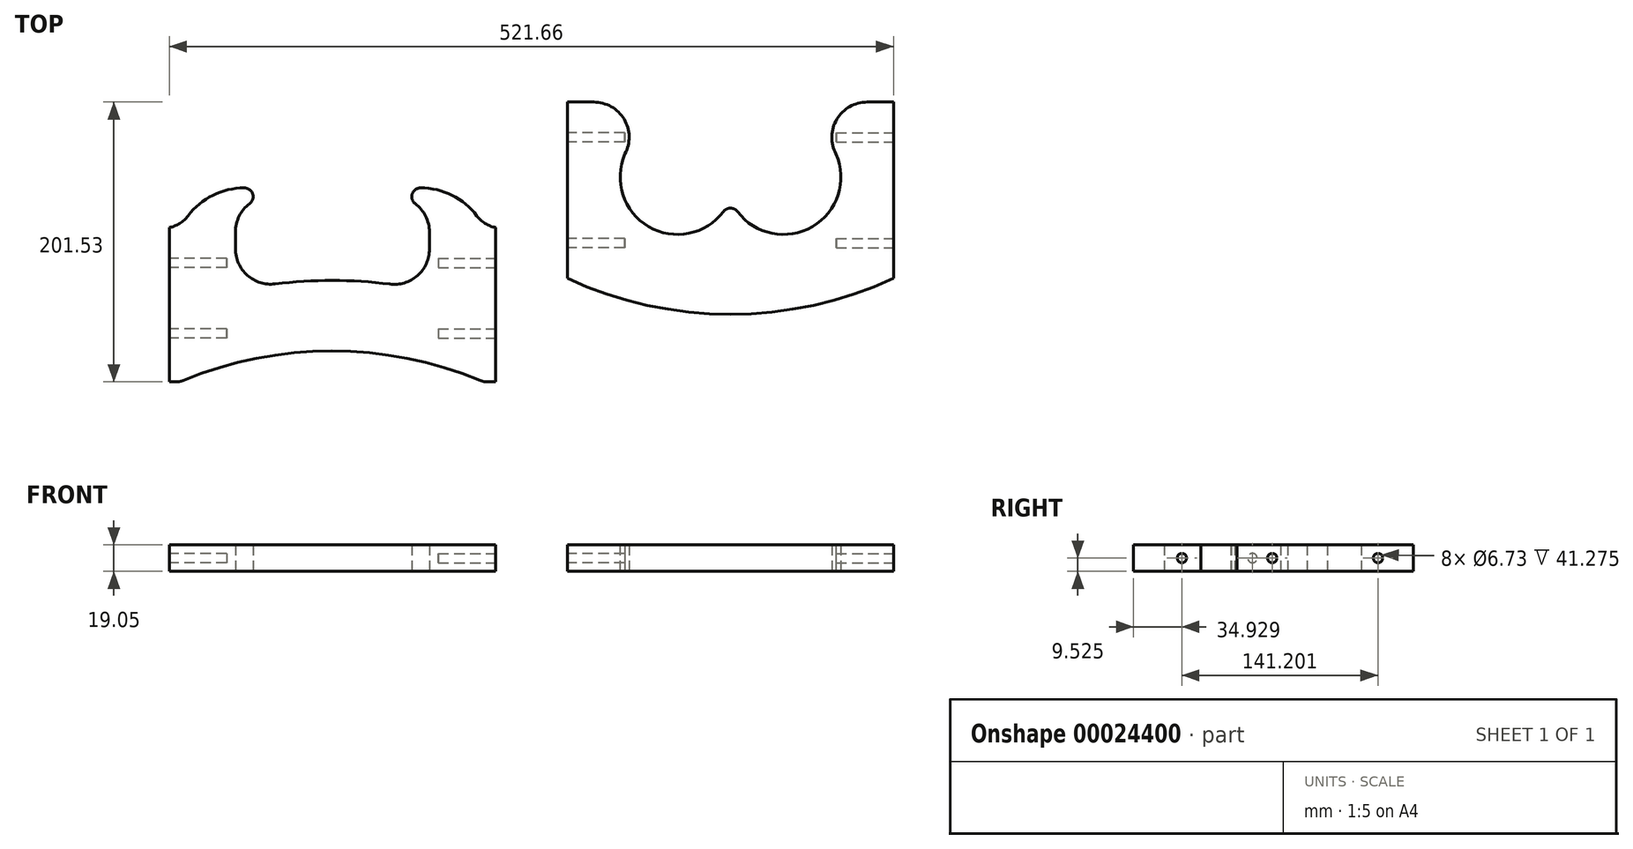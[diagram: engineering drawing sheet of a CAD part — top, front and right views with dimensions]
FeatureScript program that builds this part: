
annotation { "Feature Type Name" : "Feature", "Feature Type Description" : "" }
export const myFeature = defineFeature(function(context is Context, id is Id, definition is map)
    precondition{}
    {
        {
            var Q0;
            Q0=qCreatedBy(makeId("Top.planeOp"),FACE);
            var sketch = newSketch(context, id + "F0", { "sketchPlane" : qUnion([Q0])});
            skLineSegment(sketch, "E0.bottom", {"start": v(0, 0) * mm, "end": v(234.95, 0) * mm, "construction": true});
            skLineSegment(sketch, "E0.top", {"start": v(0, 152.4) * mm, "end": v(19.05, 152.4) * mm});
            skLineSegment(sketch, "E0.left", {"start": v(0, 0) * mm, "end": v(0, 25.4) * mm, "construction": true});
            skLineSegment(sketch, "E0.right", {"start": v(234.95, 0) * mm, "end": v(234.95, 25.4) * mm, "construction": true});
            skArc(sketch, "E1", {"start": v(41.43, 115) * mm, "mid": v(40.85, 140.04) * mm, "end": v(19.05, 152.4) * mm});
            skLineSegment(sketch, "E2", {"start": v(234.95, 143.8) * mm, "end": v(234.95, 143.8) * mm});
            skArc(sketch, "E3", {"start": v(42.52, 117.3) * mm, "mid": v(57.38, 63.35) * mm, "end": v(112.4, 73.47) * mm});
            skArc(sketch, "E4", {"start": v(122.54, 73.47) * mm, "mid": v(177.57, 63.35) * mm, "end": v(192.43, 117.3) * mm});
            skArc(sketch, "E5", {"start": v(0, 25.4) * mm, "mid": v(117.47, -0.5) * mm, "end": v(234.95, 25.4) * mm});
            skLineSegment(sketch, "E6", {"start": v(0, 25.4) * mm, "end": v(0, 143.8) * mm});
            skLineSegment(sketch, "E7", {"start": v(234.95, 25.4) * mm, "end": v(234.95, 143.8) * mm});
            skLineSegment(sketch, "E8.trimOffspring", {"start": v(215.9, 152.4) * mm, "end": v(234.95, 152.4) * mm});
            skLineSegment(sketch, "E9", {"start": v(0, 143.8) * mm, "end": v(0, 152.4) * mm});
            skArc(sketch, "E10", {"start": v(215.9, 152.4) * mm, "mid": v(194.1, 140.04) * mm, "end": v(193.52, 115) * mm});
            skLineSegment(sketch, "E11", {"start": v(234.95, 143.8) * mm, "end": v(234.95, 152.4) * mm});
            skArc(sketch, "E12", {"start": v(122.54, 73.47) * mm, "mid": v(117.48, 75.99) * mm, "end": v(112.4, 73.47) * mm});
            skLineSegment(sketch, "E13", {"start": v(117.48, 82.22) * mm, "end": v(117.48, 0) * mm, "construction": true});
            skSolve(sketch);
        }
        {
            var Q0;
            Q0 = qSketchRegion(id + "F0", true);
            extrude(context, id + "F1", {"entities" : qUnion([Q0]), "depth" : 19.05 * mm});
        }
        {
            var Q0;
            Q0=makeQuery(id+"F1.opExtrude","SWEPT_FACE",FACE,{"disambiguationData":[OSD([sQuery(id+"F0.wireOp",EDGE,"E6")])]});
            var sketch = newSketch(context, id + "F2", { "sketchPlane" : qUnion([Q0])});
            skLineSegment(sketch, "E14", {"start": v(-152.4, 9.53) * mm, "end": v(-25.4, 9.53) * mm, "construction": true});
            skCircle(sketch, "E15", {"center": v(-127, 9.53) * mm, "radius": 3.37 * mm});
            skCircle(sketch, "E16", {"center": v(-50.8, 9.53) * mm, "radius": 3.37 * mm});
            skSolve(sketch);
        }
        {
            var Q0;
            Q0=makeQuery(id+"F2.imprint","IMPRINT",FACE,{"disambiguationData":[TD([[makeQuery(id+"F2.imprint","IMPRINT",EDGE,{"derivedFrom":sQuery(id+"F2.wireOp",EDGE,"E16")}),1.0]])]});
            var Q1;
            Q1=makeQuery(id+"F2.imprint","IMPRINT",FACE,{"disambiguationData":[TD([[makeQuery(id+"F2.imprint","IMPRINT",EDGE,{"derivedFrom":sQuery(id+"F2.wireOp",EDGE,"E15")}),1.0]])]});
            var Q2;
            Q2=sQuery(id+"F2.wireOp",EDGE,"E16");
            var Q3;
            Q3=sQuery(id+"F2.wireOp",EDGE,"E15");
            extrude(context, id + "F3", {"entities" : qUnion([Q0, Q1]), "operationType" : NewBodyOperationType.REMOVE, "surfaceEntities" : qUnion([Q2, Q3]), "oppositeDirection" : true, "depth" : 41.27 * mm});
        }
        {
            var Q0;
            Q0=makeQuery(id+"F1.opExtrude","SWEPT_FACE",FACE,{"disambiguationData":[OSD([sQuery(id+"F0.wireOp",EDGE,"E7"),sQuery(id+"F0.wireOp",EDGE,"E11")])]});
            var sketch = newSketch(context, id + "F4", { "sketchPlane" : qUnion([Q0])});
            skLineSegment(sketch, "E17", {"start": v(152.4, 9.53) * mm, "end": v(25.4, 9.53) * mm, "construction": true});
            skCircle(sketch, "E18", {"center": v(127, 9.53) * mm, "radius": 3.37 * mm});
            skCircle(sketch, "E19", {"center": v(50.8, 9.52) * mm, "radius": 3.37 * mm});
            skSolve(sketch);
        }
        {
            var Q0;
            Q0=makeQuery(id+"F4.imprint","IMPRINT",FACE,{"disambiguationData":[TD([[makeQuery(id+"F4.imprint","IMPRINT",EDGE,{"derivedFrom":sQuery(id+"F4.wireOp",EDGE,"E18")}),1.0]])]});
            var Q1;
            Q1=makeQuery(id+"F4.imprint","IMPRINT",FACE,{"disambiguationData":[TD([[makeQuery(id+"F4.imprint","IMPRINT",EDGE,{"derivedFrom":sQuery(id+"F4.wireOp",EDGE,"E19")}),1.0]])]});
            extrude(context, id + "F5", {"entities" : qUnion([Q0, Q1]), "operationType" : NewBodyOperationType.REMOVE, "oppositeDirection" : true, "depth" : 41.27 * mm});
        }
        {
            var Q0;
            Q0=qCreatedBy(makeId("Top.planeOp"),FACE);
            var sketch = newSketch(context, id + "F6", { "sketchPlane" : qUnion([Q0])});
            skLineSegment(sketch, "E20.bottom", {"start": v(-286.71, -49.13) * mm, "end": v(-281.48, -49.13) * mm});
            skLineSegment(sketch, "E20.top", {"start": v(-286.71, 90.57) * mm, "end": v(-232.74, 90.57) * mm, "construction": true});
            skLineSegment(sketch, "E20.left", {"start": v(-286.71, -49.13) * mm, "end": v(-286.71, 62) * mm});
            skLineSegment(sketch, "E20.right", {"start": v(-51.76, -49.13) * mm, "end": v(-51.76, 62) * mm});
            skLineSegment(sketch, "E21", {"start": v(-286.71, 62) * mm, "end": v(-286.71, 89.56) * mm, "construction": true});
            skLineSegment(sketch, "E22", {"start": v(-51.76, 62) * mm, "end": v(-51.76, 89.56) * mm, "construction": true});
            skLineSegment(sketch, "E23.trimOffspring", {"start": v(-105.74, 90.57) * mm, "end": v(-51.76, 90.57) * mm, "construction": true});
            skLineSegment(sketch, "E24", {"start": v(-286.71, 89.56) * mm, "end": v(-286.71, 90.57) * mm});
            skLineSegment(sketch, "E25", {"start": v(-51.76, 89.56) * mm, "end": v(-51.76, 90.57) * mm});
            skLineSegment(sketch, "E26", {"start": v(-169.24, 23.9) * mm, "end": v(-169.24, -26.9) * mm, "construction": true});
            skLineSegment(sketch, "E27", {"start": v(-169.24, -26.9) * mm, "end": v(-169.24, -49.13) * mm, "construction": true});
            skArc(sketch, "E28", {"start": v(-62.82, -48.16) * mm, "mid": v(-169.72, -26.9) * mm, "end": v(-276.62, -48.16) * mm});
            skLineSegment(sketch, "E29", {"start": v(-278.93, -49.13) * mm, "end": v(-60.52, -49.13) * mm, "construction": true});
            skLineSegment(sketch, "E30", {"start": v(-57.96, -49.13) * mm, "end": v(-51.76, -49.13) * mm});
            skPoint(sketch, "E31.visualSharp", {"position": v(-278.93, -49.13) * mm});
            skArc(sketch, "E31.filletArc", {"start": v(-281.48, -49.13) * mm, "mid": v(-279, -48.88) * mm, "end": v(-276.62, -48.16) * mm});
            skPoint(sketch, "E32.visualSharp", {"position": v(-60.52, -49.13) * mm});
            skArc(sketch, "E32.filletArc", {"start": v(-62.82, -48.16) * mm, "mid": v(-60.44, -48.88) * mm, "end": v(-57.96, -49.13) * mm});
            skLineSegment(sketch, "E33", {"start": v(-239.09, 46.57) * mm, "end": v(-239.09, 58.82) * mm});
            skLineSegment(sketch, "E34", {"start": v(-99.39, 46.45) * mm, "end": v(-99.39, 58.82) * mm});
            skArc(sketch, "E35", {"start": v(-228.93, 79.14) * mm, "mid": v(-226.71, 86.23) * mm, "end": v(-232.74, 90.57) * mm});
            skArc(sketch, "E36", {"start": v(-105.74, 90.57) * mm, "mid": v(-111.76, 86.23) * mm, "end": v(-109.55, 79.14) * mm});
            skArc(sketch, "E37", {"start": v(-228.93, 79.14) * mm, "mid": v(-236.4, 70.18) * mm, "end": v(-239.09, 58.82) * mm});
            skArc(sketch, "E38", {"start": v(-99.39, 58.82) * mm, "mid": v(-102.07, 70.18) * mm, "end": v(-109.55, 79.14) * mm});
            skPoint(sketch, "E39.orphan", {"position": v(-239.09, 75.8) * mm});
            skPoint(sketch, "E40.orphan", {"position": v(-99.39, 75.3) * mm});
            skArc(sketch, "E41", {"start": v(-239.09, 46.57) * mm, "mid": v(-230.5, 27.53) * mm, "end": v(-210.54, 21.37) * mm});
            skArc(sketch, "E42", {"start": v(-128, 21.25) * mm, "mid": v(-108, 27.39) * mm, "end": v(-99.39, 46.45) * mm});
            skArc(sketch, "E43.trimOffspring", {"start": v(-128, 21.25) * mm, "mid": v(-169.27, 23.9) * mm, "end": v(-210.54, 21.37) * mm});
            skArc(sketch, "E44", {"start": v(-232.74, 90.57) * mm, "mid": v(-255.37, 85.25) * mm, "end": v(-273.26, 70.4) * mm});
            skArc(sketch, "E45", {"start": v(-65.2, 70.4) * mm, "mid": v(-83.1, 85.25) * mm, "end": v(-105.74, 90.57) * mm});
            skArc(sketch, "E46", {"start": v(-286.71, 62) * mm, "mid": v(-279.2, 64.96) * mm, "end": v(-273.26, 70.4) * mm});
            skArc(sketch, "E47", {"start": v(-65.2, 70.4) * mm, "mid": v(-59.26, 64.96) * mm, "end": v(-51.76, 62) * mm});
            skPoint(sketch, "E48.orphan", {"position": v(-278.42, 62) * mm});
            skPoint(sketch, "E49.orphan", {"position": v(-60.05, 62) * mm});
            skSolve(sketch);
        }
        {
            var Q0;
            Q0=makeQuery(id+"F6.imprint","IMPRINT",FACE,{"disambiguationData":[TD([[makeQuery(id+"F6.imprint","IMPRINT",EDGE,{"derivedFrom":sQuery(id+"F6.wireOp",EDGE,"E20.bottom")}),1.0]])]});
            extrude(context, id + "F7", {"entities" : qUnion([Q0]), "depth" : 19.05 * mm});
        }
        {
            var Q0;
            Q0=makeQuery(id+"F7.opExtrude","SWEPT_FACE",FACE,{"disambiguationData":[OSD([sQuery(id+"F6.wireOp",EDGE,"E20.left")])]});
            var sketch = newSketch(context, id + "F8", { "sketchPlane" : qUnion([Q0])});
            skLineSegment(sketch, "E50", {"start": v(-62, 9.53) * mm, "end": v(49.13, 9.53) * mm, "construction": true});
            skCircle(sketch, "E51", {"center": v(-36.6, 9.52) * mm, "radius": 3.37 * mm});
            skCircle(sketch, "E52", {"center": v(14.2, 9.53) * mm, "radius": 3.37 * mm});
            skSolve(sketch);
        }
        {
            var Q0;
            Q0=makeQuery(id+"F7.opExtrude","SWEPT_FACE",FACE,{"disambiguationData":[OSD([sQuery(id+"F6.wireOp",EDGE,"E20.right")])]});
            var sketch = newSketch(context, id + "F9", { "sketchPlane" : qUnion([Q0])});
            skLineSegment(sketch, "E53", {"start": v(62, 9.53) * mm, "end": v(-49.13, 9.53) * mm, "construction": true});
            skCircle(sketch, "E54", {"center": v(36.6, 9.53) * mm, "radius": 3.37 * mm});
            skCircle(sketch, "E55", {"center": v(-14.2, 9.52) * mm, "radius": 3.37 * mm});
            skSolve(sketch);
        }
        {
            var Q0;
            Q0=makeQuery(id+"F9.imprint","IMPRINT",FACE,{"disambiguationData":[TD([[makeQuery(id+"F9.imprint","IMPRINT",EDGE,{"derivedFrom":sQuery(id+"F9.wireOp",EDGE,"E55")}),1.0]])]});
            var Q1;
            Q1=makeQuery(id+"F9.imprint","IMPRINT",FACE,{"disambiguationData":[TD([[makeQuery(id+"F9.imprint","IMPRINT",EDGE,{"derivedFrom":sQuery(id+"F9.wireOp",EDGE,"E54")}),1.0]])]});
            extrude(context, id + "F10", {"entities" : qUnion([Q0, Q1]), "operationType" : NewBodyOperationType.REMOVE, "oppositeDirection" : true, "depth" : 41.27 * mm});
        }
        {
            var Q0;
            Q0=makeQuery(id+"F8.imprint","IMPRINT",FACE,{"disambiguationData":[TD([[makeQuery(id+"F8.imprint","IMPRINT",EDGE,{"derivedFrom":sQuery(id+"F8.wireOp",EDGE,"E52")}),1.0]])]});
            var Q1;
            Q1=makeQuery(id+"F8.imprint","IMPRINT",FACE,{"disambiguationData":[TD([[makeQuery(id+"F8.imprint","IMPRINT",EDGE,{"derivedFrom":sQuery(id+"F8.wireOp",EDGE,"E51")}),1.0]])]});
            extrude(context, id + "F11", {"entities" : qUnion([Q0, Q1]), "operationType" : NewBodyOperationType.REMOVE, "oppositeDirection" : true, "depth" : 41.27 * mm});
        }
    });
